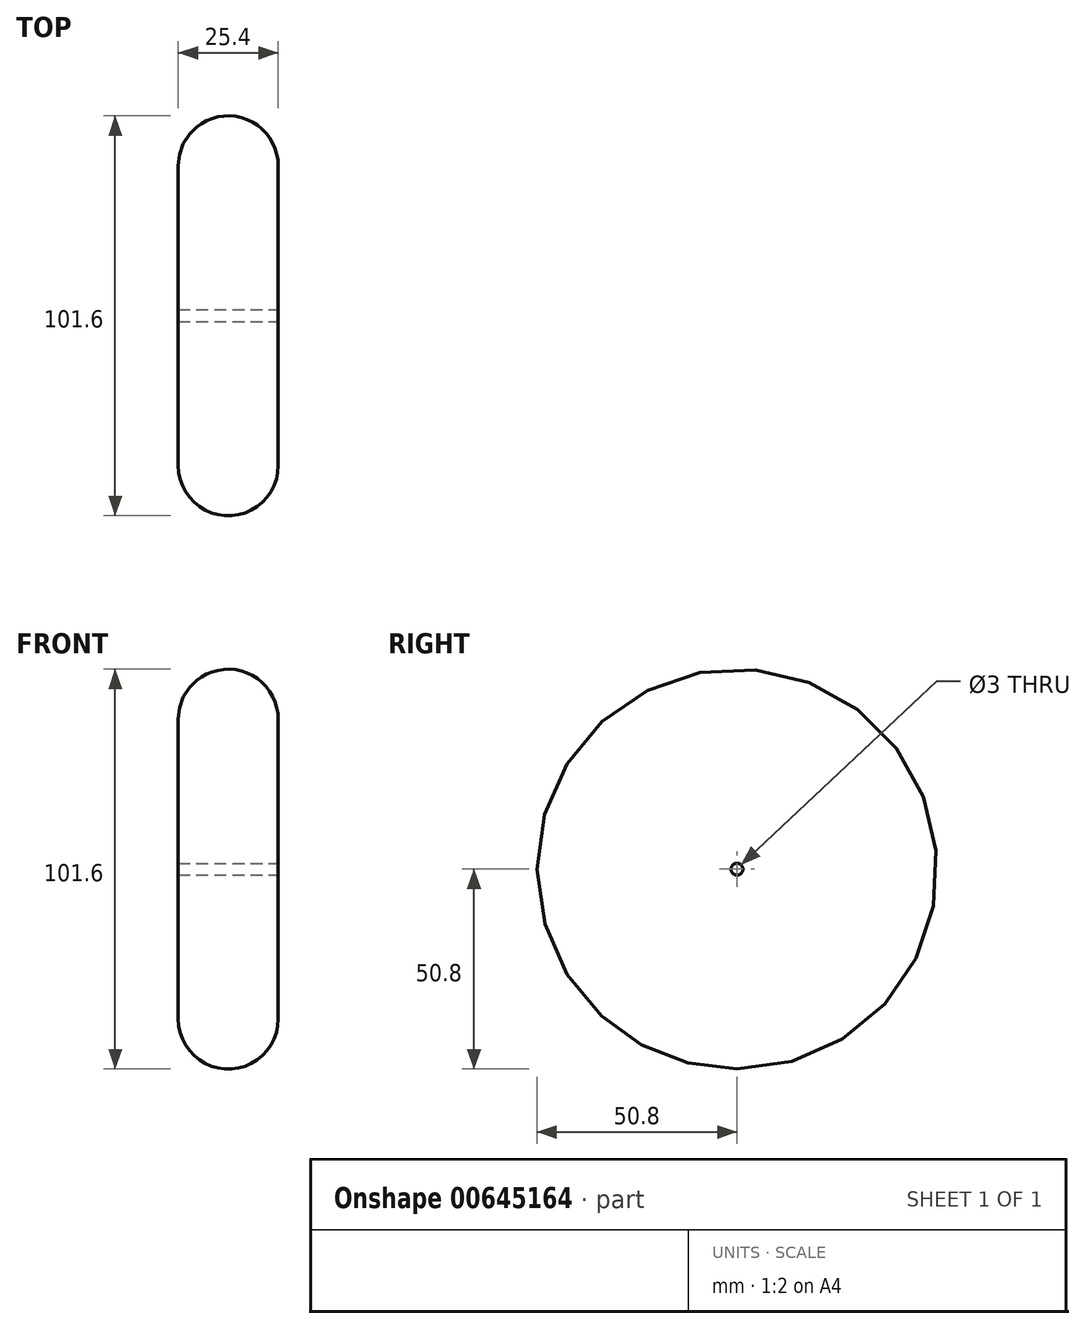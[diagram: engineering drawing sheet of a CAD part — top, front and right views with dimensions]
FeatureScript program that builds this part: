
annotation { "Feature Type Name" : "Feature", "Feature Type Description" : "" }
export const myFeature = defineFeature(function(context is Context, id is Id, definition is map)
    precondition{}
    {
        {
            var Q0;
            Q0=qCreatedBy(makeId("Right.planeOp"),FACE);
            var sketch = newSketch(context, id + "F0", { "sketchPlane" : qUnion([Q0])});
            skCircle(sketch, "E0", {"center": v(0, 0) * mm, "radius": 50.8 * mm});
            skSolve(sketch);
        }
        {
            var Q0;
            Q0=makeQuery(id+"F0.imprint","IMPRINT",FACE,{"disambiguationData":[TD([[makeQuery(id+"F0.imprint","IMPRINT",EDGE,{"derivedFrom":sQuery(id+"F0.wireOp",EDGE,"E0")}),1.0]])]});
            extrude(context, id + "F1", {"entities" : qUnion([Q0]), "depth" : 25.4 * mm, "offsetDistance" : 25.4 * mm});
        }
        {
            var Q0;
            Q0=makeQuery(id+"F1.opExtrude","CAP_EDGE",EDGE,{"disambiguationData":[OSD([sQuery(id+"F0.wireOp",EDGE,"E0")])],"isStart":false});
            fillet(context, id + "F2", {"entities" : qUnion([Q0]), "radius" : 12.7 * mm, "tangentPropagation" : true, "allowEdgeOverflow" : false});
        }
        {
            var Q0;
            Q0=makeQuery(id+"F1.opExtrude","CAP_EDGE",EDGE,{"disambiguationData":[OSD([sQuery(id+"F0.wireOp",EDGE,"E0")])],"isStart":true});
            fillet(context, id + "F3", {"entities" : qUnion([Q0]), "radius" : 12.7 * mm, "tangentPropagation" : true, "allowEdgeOverflow" : false});
        }
        {
            var Q0;
            Q0=makeQuery(id+"F1.opExtrude","CAP_FACE",FACE,{"disambiguationData":[OSD([sQuery(id+"F0.wireOp",EDGE,"E0")])],"isStart":false});
            var sketch = newSketch(context, id + "F4", { "sketchPlane" : qUnion([Q0])});
            skCircle(sketch, "E1", {"center": v(0, 0) * mm, "radius": 3.17 * mm});
            skSolve(sketch);
        }
        {
            var Q0;
            Q0=sQuery(id+"F4.wireOp",VERTEX,"E1.center");
            var Q1;
            Q1=makeQuery(id+"F1.opExtrude","SWEPT_BODY",BODY,{"disambiguationData":[OSD([sQuery(id+"F0.wireOp",EDGE,"E0")])]});
            hole(context, id + "F5", {"style" : HoleStyle.SIMPLE, "endStyle" : HoleEndStyle.THROUGH, "holeDiameter" : 3 * mm, "majorDiameter" : 6.35 * mm, "isTappedThrough" : true, "tappedDepth" : 12.7 * mm, "tapClearance" : 3, "locations" : qUnion([Q0]), "scope" : qUnion([Q1])});
        }
    });
